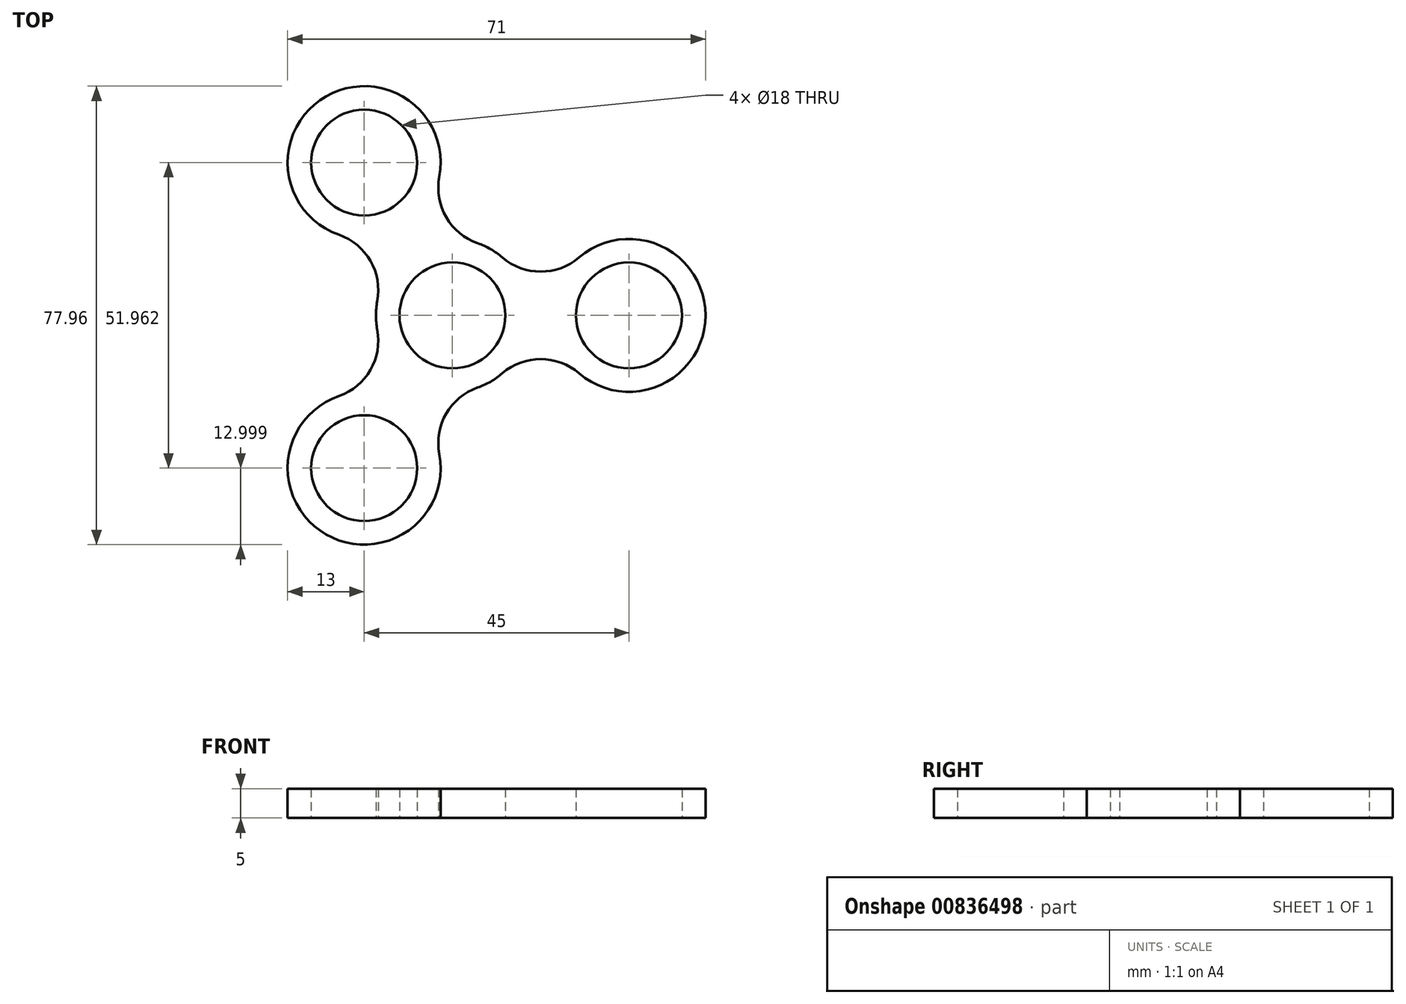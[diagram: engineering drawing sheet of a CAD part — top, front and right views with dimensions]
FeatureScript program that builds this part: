
annotation { "Feature Type Name" : "Feature", "Feature Type Description" : "" }
export const myFeature = defineFeature(function(context is Context, id is Id, definition is map)
    precondition{}
    {
        {
            var Q0;
            Q0=qCreatedBy(makeId("Top.planeOp"),FACE);
            var sketch = newSketch(context, id + "F0", { "sketchPlane" : qUnion([Q0])});
            skCircle(sketch, "E0", {"center": v(30, 0) * mm, "radius": 9 * mm});
            skCircle(sketch, "E1", {"center": v(0, 0) * mm, "radius": 9 * mm});
            skCircle(sketch, "E2.1.0", {"center": v(-15, 25.98) * mm, "radius": 9 * mm});
            skCircle(sketch, "E2.2.0", {"center": v(-15, -25.98) * mm, "radius": 9 * mm});
            skCircle(sketch, "E3", {"center": v(0, 0) * mm, "radius": 13 * mm});
            skCircle(sketch, "E4", {"center": v(30, 0) * mm, "radius": 13 * mm});
            skArc(sketch, "E5", {"start": v(8.48, 9.85) * mm, "mid": v(15, 7.44) * mm, "end": v(21.52, 9.85) * mm});
            skArc(sketch, "E6", {"start": v(21.52, -9.85) * mm, "mid": v(15, -7.44) * mm, "end": v(8.48, -9.85) * mm});
            skArc(sketch, "E7.1.0", {"start": v(-2.23, 23.57) * mm, "mid": v(-1.06, 16.7) * mm, "end": v(4.3, 12.27) * mm});
            skArc(sketch, "E7.1.1", {"start": v(-12.77, 2.41) * mm, "mid": v(-13.94, 9.27) * mm, "end": v(-19.3, 13.71) * mm});
            skCircle(sketch, "E7.1.2", {"center": v(-15, 25.98) * mm, "radius": 13 * mm});
            skArc(sketch, "E7.2.0", {"start": v(-19.3, -13.71) * mm, "mid": v(-13.94, -9.27) * mm, "end": v(-12.77, -2.41) * mm});
            skArc(sketch, "E7.2.1", {"start": v(4.3, -12.27) * mm, "mid": v(-1.06, -16.7) * mm, "end": v(-2.23, -23.57) * mm});
            skCircle(sketch, "E7.2.2", {"center": v(-15, -25.98) * mm, "radius": 13 * mm});
            skSolve(sketch);
        }
        {
            var Q0;
            Q0=makeQuery(id+"F0.imprint","IMPRINT",FACE,{"disambiguationData":[TD([[makeQuery(id+"F0.imprint","IMPRINT",EDGE,{"derivedFrom":sQuery(id+"F0.wireOp",EDGE,"E2.1.0")}),-1.0]])]});
            var Q1;
            Q1=makeQuery(id+"F0.imprint","IMPRINT",FACE,{"disambiguationData":[TD([[makeQuery(id+"F0.imprint","IMPRINT",EDGE,{"derivedFrom":sQuery(id+"F0.wireOp",EDGE,"E1")}),-1.0]])]});
            var Q2;
            {var subQ0=sQuery(id+"F0.wireOp",EDGE,"E7.1.0");Q2=makeQuery(id+"F0.imprint","IMPRINT",FACE,{"disambiguationData":[TD([[makeQuery(id+"F0.imprint","IMPRINT",EDGE,{"derivedFrom":subQ0}),-1.0]])]});}
            var Q3;
            {var subQ0=sQuery(id+"F0.wireOp",EDGE,"E5");Q3=makeQuery(id+"F0.imprint","IMPRINT",FACE,{"disambiguationData":[TD([[makeQuery(id+"F0.imprint","IMPRINT",EDGE,{"derivedFrom":subQ0}),-1.0]])]});}
            var Q4;
            Q4=makeQuery(id+"F0.imprint","IMPRINT",FACE,{"disambiguationData":[TD([[makeQuery(id+"F0.imprint","IMPRINT",EDGE,{"derivedFrom":sQuery(id+"F0.wireOp",EDGE,"E0")}),-1.0]])]});
            var Q5;
            {var subQ0=sQuery(id+"F0.wireOp",EDGE,"E7.2.0");Q5=makeQuery(id+"F0.imprint","IMPRINT",FACE,{"disambiguationData":[TD([[makeQuery(id+"F0.imprint","IMPRINT",EDGE,{"derivedFrom":subQ0}),-1.0]])]});}
            var Q6;
            Q6=makeQuery(id+"F0.imprint","IMPRINT",FACE,{"disambiguationData":[TD([[makeQuery(id+"F0.imprint","IMPRINT",EDGE,{"derivedFrom":sQuery(id+"F0.wireOp",EDGE,"E2.2.0")}),-1.0]])]});
            extrude(context, id + "F1", {"entities" : qUnion([Q0, Q1, Q2, Q3, Q4, Q5, Q6]), "depth" : 5 * mm, "offsetDistance" : 25 * mm});
        }
    });
